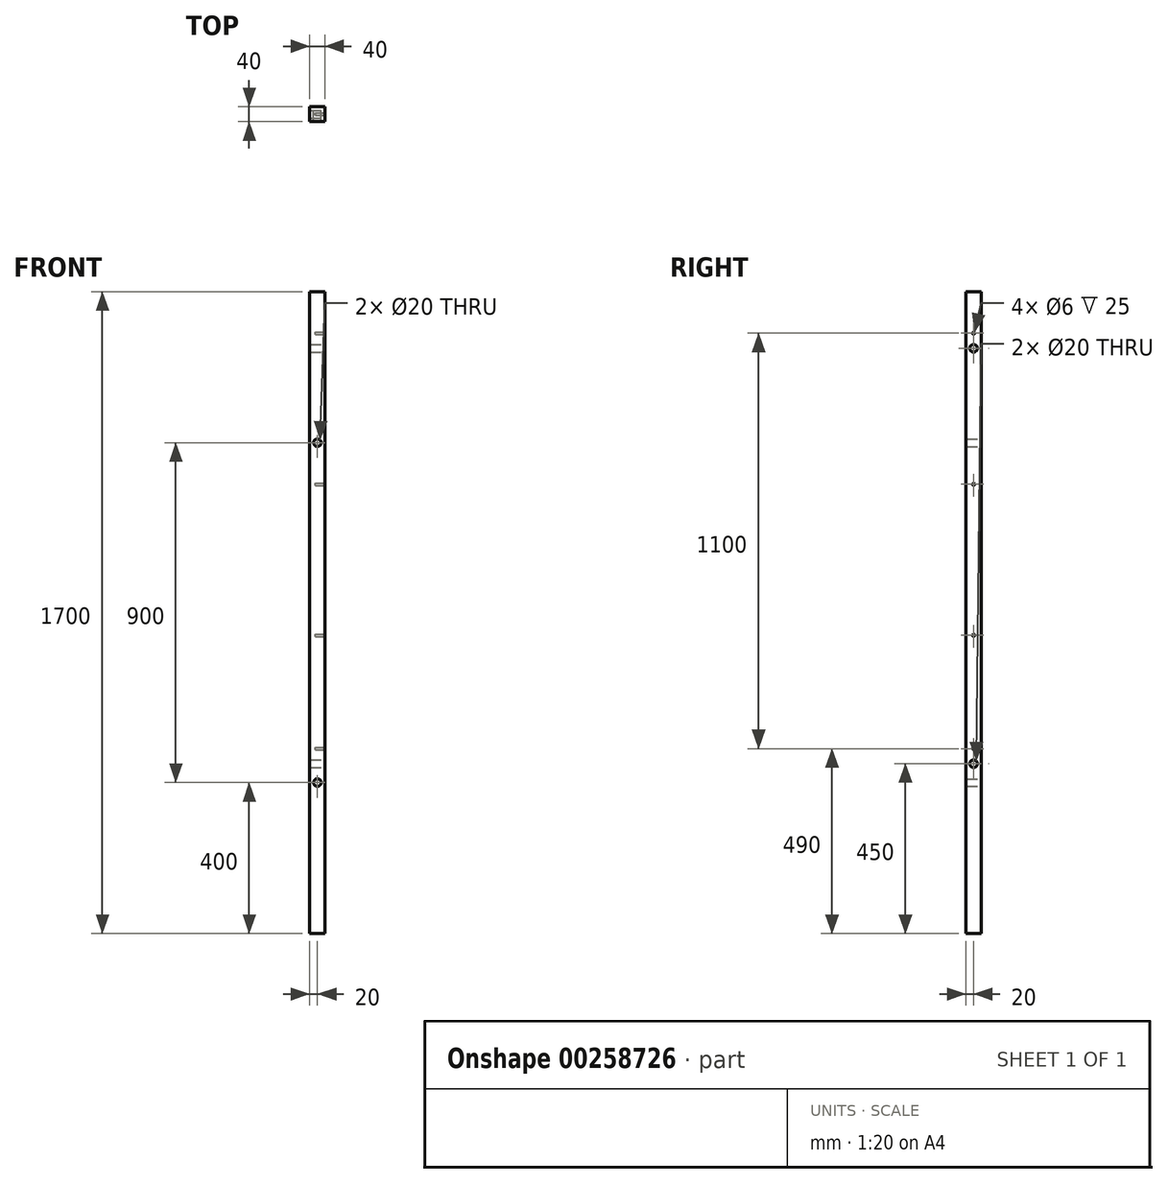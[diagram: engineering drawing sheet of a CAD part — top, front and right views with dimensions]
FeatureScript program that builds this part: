
annotation { "Feature Type Name" : "Feature", "Feature Type Description" : "" }
export const myFeature = defineFeature(function(context is Context, id is Id, definition is map)
    precondition{}
    {
        {
            var Q0;
            Q0=qCreatedBy(makeId("Front.planeOp"),FACE);
            var sketch = newSketch(context, id + "F0", { "sketchPlane" : qUnion([Q0])});
            skLineSegment(sketch, "E0.bottom", {"start": v(-40, 0) * mm, "end": v(0, 0) * mm});
            skLineSegment(sketch, "E0.top", {"start": v(-40, 1700) * mm, "end": v(0, 1700) * mm});
            skLineSegment(sketch, "E0.left", {"start": v(-40, 0) * mm, "end": v(-40, 1700) * mm});
            skLineSegment(sketch, "E0.right", {"start": v(0, 0) * mm, "end": v(0, 1700) * mm});
            skCircle(sketch, "E1", {"center": v(-20, 400) * mm, "radius": 10 * mm});
            skPoint(sketch, "E1.centerSnap0", {"position": v(-20, 0) * mm});
            skPoint(sketch, "E2.centerSnap0", {"position": v(0, 850) * mm});
            skCircle(sketch, "E3", {"center": v(-20, 1300) * mm, "radius": 10 * mm});
            skPoint(sketch, "E3.centerSnap0", {"position": v(-20, 1700) * mm});
            skSolve(sketch);
        }
        {
            var Q0;
            Q0=makeQuery(id+"F0.imprint","IMPRINT",FACE,{"disambiguationData":[TD([[makeQuery(id+"F0.imprint","IMPRINT",EDGE,{"derivedFrom":sQuery(id+"F0.wireOp",EDGE,"E0.bottom")}),1.0]])]});
            extrude(context, id + "F1", {"entities" : qUnion([Q0]), "depth" : 40 * mm});
        }
        {
            var Q0;
            Q0=makeQuery(id+"F1.opExtrude","SWEPT_FACE",FACE,{"disambiguationData":[OSD([sQuery(id+"F0.wireOp",EDGE,"E0.right")])]});
            var sketch = newSketch(context, id + "F7", { "sketchPlane" : qUnion([Q0])});
            skLineSegment(sketch, "E4.0", {"start": v(-40, 0) * mm, "end": v(-40, 1700) * mm});
            skLineSegment(sketch, "E5.0", {"start": v(0, 0) * mm, "end": v(0, 1700) * mm});
            skLineSegment(sketch, "E6.0", {"start": v(-40, 0) * mm, "end": v(0, 0) * mm});
            skLineSegment(sketch, "E7.0", {"start": v(-40, 1700) * mm, "end": v(0, 1700) * mm});
            skCircle(sketch, "E8", {"center": v(-20, 450) * mm, "radius": 10 * mm});
            skLineSegment(sketch, "E9", {"start": v(0, 390) * mm, "end": v(-40, 390) * mm});
            skLineSegment(sketch, "E10", {"start": v(-40, 410) * mm, "end": v(0, 410) * mm});
            skLineSegment(sketch, "E11.0", {"start": v(-40, 1290) * mm, "end": v(-40, 1310) * mm});
            skPoint(sketch, "E12.1", {"position": v(0, 1300) * mm});
            skLineSegment(sketch, "E12.2.1", {"start": v(-40, 1700) * mm, "end": v(-40, 0) * mm});
            skLineSegment(sketch, "E12.3.0", {"start": v(0, 1700) * mm, "end": v(0, 0) * mm});
            skLineSegment(sketch, "E12.3.1", {"start": v(0, 0) * mm, "end": v(-40, 0) * mm});
            skLineSegment(sketch, "E12.4", {"start": v(0, 1290) * mm, "end": v(0, 1310) * mm});
            skCircle(sketch, "E13", {"center": v(-20, 1550) * mm, "radius": 10 * mm});
            skCircle(sketch, "E14", {"center": v(-20, 490) * mm, "radius": 3 * mm});
            skCircle(sketch, "E15", {"center": v(-20, 790) * mm, "radius": 3 * mm});
            skCircle(sketch, "E16", {"center": v(-20, 1190) * mm, "radius": 3 * mm});
            skCircle(sketch, "E17", {"center": v(-20, 1590) * mm, "radius": 3 * mm});
            skSolve(sketch);
        }
        {
            var Q0;
            Q0=makeQuery(id+"F7.imprint","IMPRINT",FACE,{"disambiguationData":[TD([[makeQuery(id+"F7.imprint","IMPRINT",EDGE,{"derivedFrom":sQuery(id+"F7.wireOp",EDGE,"E8")}),1.0]])]});
            var Q1;
            Q1=sQuery(id+"F7.wireOp",EDGE,"E8");
            extrude(context, id + "F2", {"entities" : qUnion([Q0]), "operationType" : NewBodyOperationType.REMOVE, "surfaceEntities" : qUnion([Q1]), "endBound" : BoundingType.THROUGH_ALL, "oppositeDirection" : true, "depth" : 25 * mm});
        }
        {
            var Q0;
            Q0=makeQuery(id+"F7.imprint","IMPRINT",FACE,{"disambiguationData":[TD([[makeQuery(id+"F7.imprint","IMPRINT",EDGE,{"derivedFrom":sQuery(id+"F7.wireOp",EDGE,"E13")}),1.0]])]});
            var Q1;
            Q1=sQuery(id+"F7.wireOp",EDGE,"E13");
            extrude(context, id + "F3", {"entities" : qUnion([Q0]), "operationType" : NewBodyOperationType.REMOVE, "surfaceEntities" : qUnion([Q1]), "endBound" : BoundingType.THROUGH_ALL, "oppositeDirection" : true, "depth" : 25 * mm});
        }
        {
            var Q0;
            Q0=makeQuery(id+"F7.imprint","IMPRINT",FACE,{"disambiguationData":[TD([[makeQuery(id+"F7.imprint","IMPRINT",EDGE,{"derivedFrom":sQuery(id+"F7.wireOp",EDGE,"E14")}),1.0]])]});
            extrude(context, id + "F4", {"entities" : qUnion([Q0]), "operationType" : NewBodyOperationType.REMOVE, "oppositeDirection" : true, "depth" : 25 * mm});
        }
        {
            var Q0;
            Q0=makeQuery(id+"F7.imprint","IMPRINT",FACE,{"disambiguationData":[TD([[makeQuery(id+"F7.imprint","IMPRINT",EDGE,{"derivedFrom":sQuery(id+"F7.wireOp",EDGE,"E15")}),1.0]])]});
            extrude(context, id + "F8", {"entities" : qUnion([Q0]), "operationType" : NewBodyOperationType.REMOVE, "oppositeDirection" : true, "depth" : 25 * mm});
        }
        {
            var Q0;
            Q0=makeQuery(id+"F7.imprint","IMPRINT",FACE,{"disambiguationData":[TD([[makeQuery(id+"F7.imprint","IMPRINT",EDGE,{"derivedFrom":sQuery(id+"F7.wireOp",EDGE,"E16")}),1.0]])]});
            extrude(context, id + "F5", {"entities" : qUnion([Q0]), "operationType" : NewBodyOperationType.REMOVE, "oppositeDirection" : true, "depth" : 25 * mm});
        }
        {
            var Q0;
            Q0=makeQuery(id+"F7.imprint","IMPRINT",FACE,{"disambiguationData":[TD([[makeQuery(id+"F7.imprint","IMPRINT",EDGE,{"derivedFrom":sQuery(id+"F7.wireOp",EDGE,"E17")}),1.0]])]});
            extrude(context, id + "F6", {"entities" : qUnion([Q0]), "operationType" : NewBodyOperationType.REMOVE, "oppositeDirection" : true, "depth" : 25 * mm});
        }
    });
